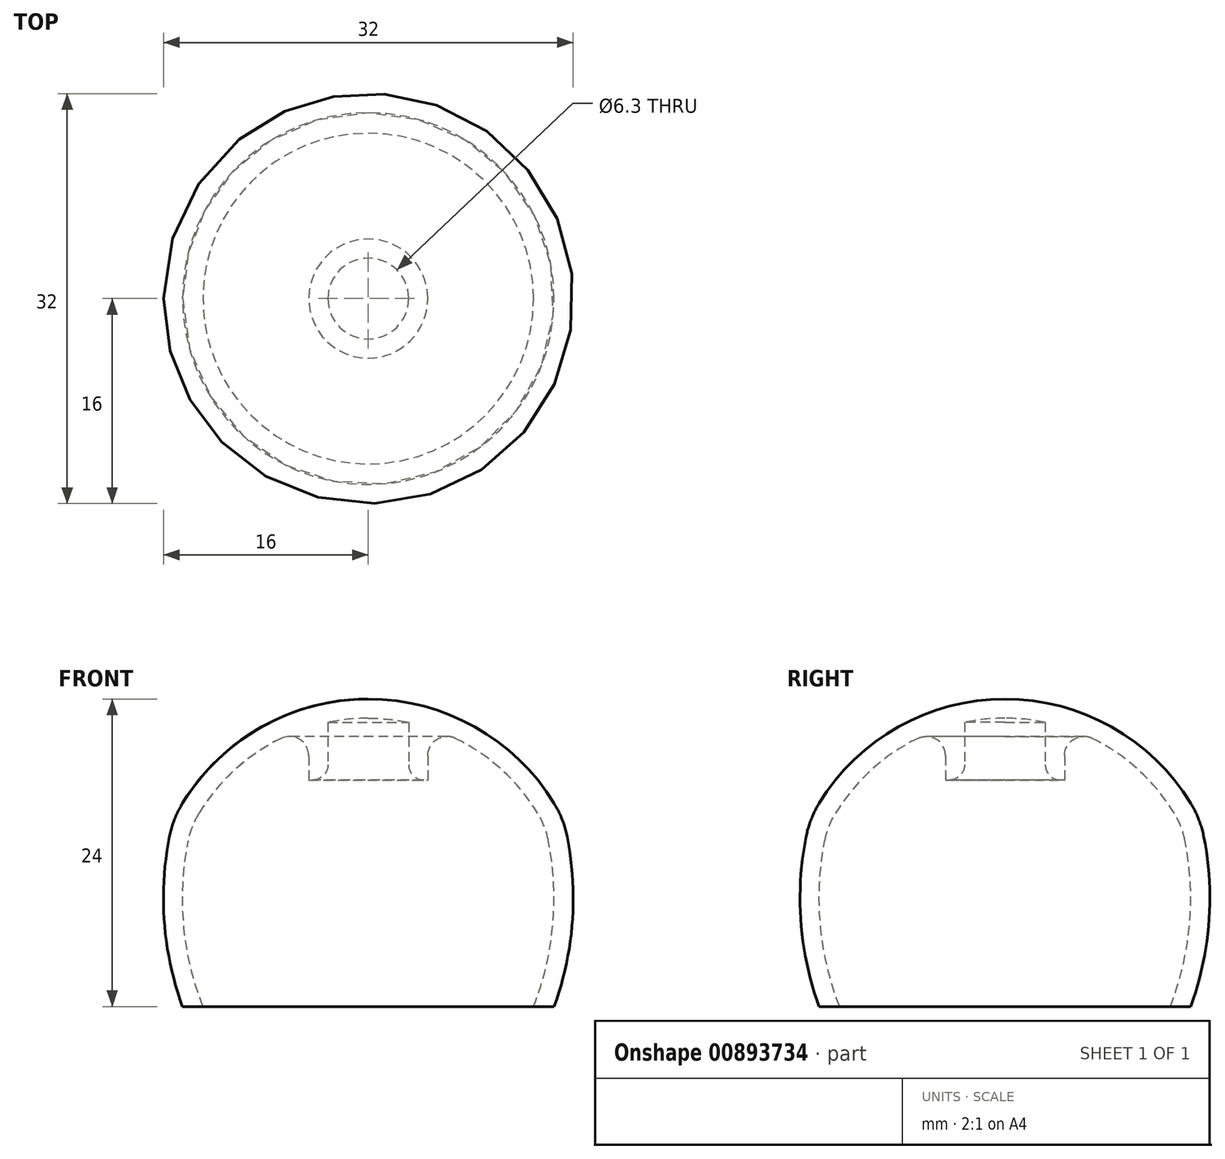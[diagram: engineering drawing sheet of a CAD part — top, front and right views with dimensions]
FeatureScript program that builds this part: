
annotation { "Feature Type Name" : "Feature", "Feature Type Description" : "" }
export const myFeature = defineFeature(function(context is Context, id is Id, definition is map)
    precondition{}
    {
        {
            var Q0;
            Q0=qCreatedBy(makeId("Front.planeOp"),FACE);
            var sketch = newSketch(context, id + "F0", { "sketchPlane" : qUnion([Q0])});
            skLineSegment(sketch, "E0", {"start": v(-4.65, 21.79) * mm, "end": v(-4.65, 17.68) * mm});
            skLineSegment(sketch, "E1", {"start": v(-4.65, 17.68) * mm, "end": v(-3.15, 17.68) * mm});
            skLineSegment(sketch, "E2", {"start": v(-3.15, 17.68) * mm, "end": v(-3.15, 22.18) * mm});
            skLineSegment(sketch, "E3", {"start": v(0, 24) * mm, "end": v(-16, 24) * mm, "construction": true});
            skLineSegment(sketch, "E4", {"start": v(-16, 24) * mm, "end": v(-16, 0) * mm, "construction": true});
            skArc(sketch, "E5", {"start": v(0, 24) * mm, "mid": v(-8.32, 21.83) * mm, "end": v(-14.51, 15.86) * mm});
            skArc(sketch, "E6", {"start": v(-14.51, 15.86) * mm, "mid": v(-15.14, 14.6) * mm, "end": v(-15.53, 13.24) * mm});
            skArc(sketch, "E7", {"start": v(-15.53, 13.24) * mm, "mid": v(-15.93, 6.55) * mm, "end": v(-14.51, 0) * mm});
            skLineSegment(sketch, "E8", {"start": v(-14.51, 0) * mm, "end": v(40.06, 19.86) * mm, "construction": true});
            skLineSegment(sketch, "E9", {"start": v(-15.53, 13.24) * mm, "end": v(37.56, 2.73) * mm, "construction": true});
            skLineSegment(sketch, "E10", {"start": v(-14.51, 15.86) * mm, "end": v(35.06, -14.4) * mm, "construction": true});
            skLineSegment(sketch, "E11", {"start": v(40.06, 19.86) * mm, "end": v(35.06, -14.4) * mm, "construction": true});
            skPoint(sketch, "E12", {"position": v(37.56, 2.73) * mm});
            skArc(sketch, "E13.0", {"start": v(-14.06, 12.95) * mm, "mid": v(-14.4, 6.4) * mm, "end": v(-12.9, 0) * mm});
            skArc(sketch, "E13.1", {"start": v(-13.23, 15.08) * mm, "mid": v(-13.74, 14.05) * mm, "end": v(-14.06, 12.95) * mm});
            skArc(sketch, "E13.2", {"start": v(0, 22.5) * mm, "mid": v(-7.59, 20.52) * mm, "end": v(-13.23, 15.08) * mm});
            skLineSegment(sketch, "E14", {"start": v(0, 22.5) * mm, "end": v(0, 24) * mm});
            skLineSegment(sketch, "E15", {"start": v(-12.9, 0) * mm, "end": v(-14.51, 0) * mm});
            skSolve(sketch);
        }
        {
            var Q0;
            Q0=qSketchRegion(id+"F0",true);
            var Q1;
            Q1=sQuery(id+"F0.wireOp",EDGE,"E14");
            revolve(context, id + "F1", {"surfaceOperationType" : NewSurfaceOperationType.NEW, "entities" : qUnion([Q0]), "axis" : qUnion([Q1]), "revolveType" : RevolveType.FULL});
        }
        {
            var Q0;
            Q0=makeQuery(id+"F1.opRevolve","SWEPT_EDGE",EDGE,{"disambiguationData":[OSD([sQuery(id+"F0.wireOp",EDGE,"E1"),sQuery(id+"F0.wireOp",EDGE,"E2")])]});
            fillet(context, id + "F2", {"entities" : qUnion([Q0]), "radius" : 1.2 * mm, "tangentPropagation" : true, "allowEdgeOverflow" : false});
        }
        {
            var Q0;
            Q0=makeQuery(id+"F1.opRevolve","SWEPT_EDGE",EDGE,{"disambiguationData":[OSD([sQuery(id+"F0.wireOp",EDGE,"E0"),sQuery(id+"F0.wireOp",EDGE,"E13.2")])]});
            fillet(context, id + "F3", {"entities" : qUnion([Q0]), "radius" : 1.5 * mm, "tangentPropagation" : true, "allowEdgeOverflow" : false});
        }
    });
